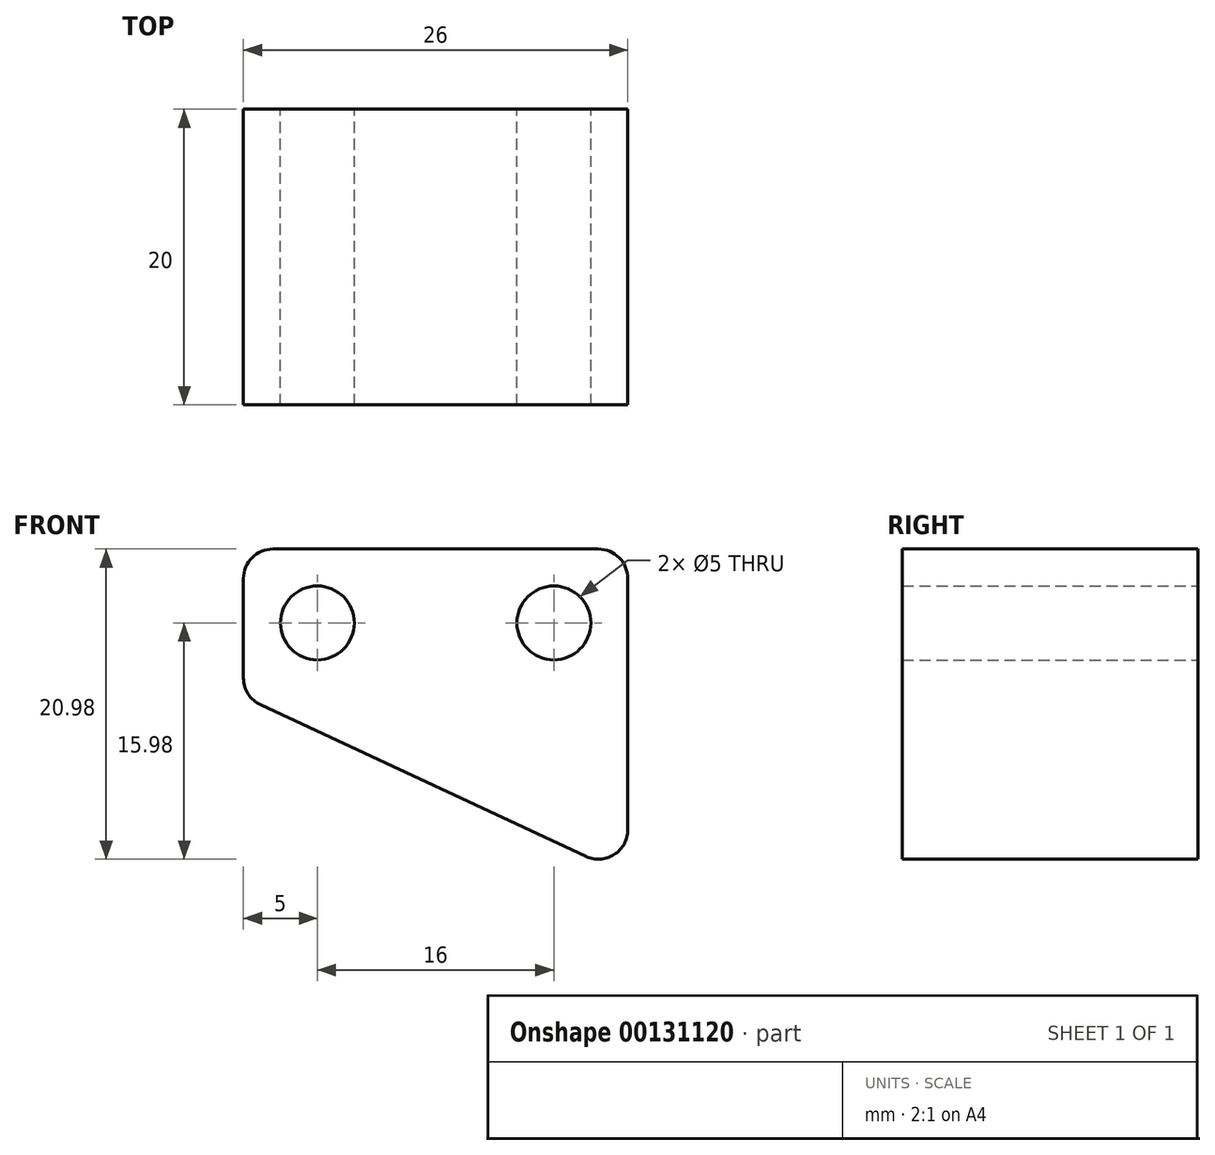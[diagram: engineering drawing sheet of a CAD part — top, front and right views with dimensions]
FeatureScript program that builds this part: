
annotation { "Feature Type Name" : "Feature", "Feature Type Description" : "" }
export const myFeature = defineFeature(function(context is Context, id is Id, definition is map)
    precondition{}
    {
        {
            var Q0;
            Q0=qCreatedBy(makeId("Front.planeOp"),FACE);
            var sketch = newSketch(context, id + "F0", { "sketchPlane" : qUnion([Q0])});
            skLineSegment(sketch, "E0", {"start": v(0, 0) * mm, "end": v(26, 0) * mm});
            skLineSegment(sketch, "E1", {"start": v(26, 0) * mm, "end": v(26, -22.12) * mm});
            skLineSegment(sketch, "E2", {"start": v(26, -22.12) * mm, "end": v(0, -10) * mm});
            skLineSegment(sketch, "E3", {"start": v(0, -10) * mm, "end": v(0, 0) * mm});
            skLineSegment(sketch, "E4", {"start": v(0, -5) * mm, "end": v(26, -5) * mm, "construction": true});
            skPoint(sketch, "E5", {"position": v(5, -5) * mm});
            skPoint(sketch, "E6", {"position": v(21, -5) * mm});
            skSolve(sketch);
        }
        {
            var Q0;
            Q0=makeQuery(id+"F0.imprint","IMPRINT",FACE,{"disambiguationData":[TD([[makeQuery(id+"F0.imprint","IMPRINT",EDGE,{"derivedFrom":sQuery(id+"F0.wireOp",EDGE,"E0")}),-1.0]])]});
            extrude(context, id + "F1", {"entities" : qUnion([Q0]), "depth" : 20 * mm});
        }
        {
            var Q0;
            Q0=sQuery(id+"F0.wireOp",VERTEX,"E5");
            var Q1;
            Q1=sQuery(id+"F0.wireOp",VERTEX,"E6");
            var Q2;
            Q2=makeQuery(id+"F1.opExtrude","SWEPT_BODY",BODY,{"disambiguationData":[OSD([sQuery(id+"F0.wireOp",EDGE,"E0"),sQuery(id+"F0.wireOp",EDGE,"E1"),sQuery(id+"F0.wireOp",EDGE,"E2"),sQuery(id+"F0.wireOp",EDGE,"E3")])]});
            hole(context, id + "F2", {"style" : HoleStyle.SIMPLE, "endStyle" : HoleEndStyle.THROUGH, "oppositeDirection" : true, "holeDiameter" : 5 * mm, "locations" : qUnion([Q0, Q1]), "scope" : qUnion([Q2]), "isTappedThrough" : true});
        }
        {
            var Q0;
            Q0=makeQuery(id+"F1.opExtrude","SWEPT_EDGE",EDGE,{"disambiguationData":[OSD([sQuery(id+"F0.wireOp",EDGE,"E1"),sQuery(id+"F0.wireOp",EDGE,"E2")])]});
            var Q1;
            Q1=makeQuery(id+"F1.opExtrude","SWEPT_EDGE",EDGE,{"disambiguationData":[OSD([sQuery(id+"F0.wireOp",EDGE,"E2"),sQuery(id+"F0.wireOp",EDGE,"E3")])]});
            var Q2;
            Q2=makeQuery(id+"F1.opExtrude","SWEPT_EDGE",EDGE,{"disambiguationData":[OSD([sQuery(id+"F0.wireOp",EDGE,"E0"),sQuery(id+"F0.wireOp",EDGE,"E3")])]});
            var Q3;
            Q3=makeQuery(id+"F1.opExtrude","SWEPT_EDGE",EDGE,{"disambiguationData":[OSD([sQuery(id+"F0.wireOp",EDGE,"E0"),sQuery(id+"F0.wireOp",EDGE,"E1")])]});
            fillet(context, id + "F3", {"entities" : qUnion([Q0, Q1, Q2, Q3]), "radius" : 2 * mm, "tangentPropagation" : true, "allowEdgeOverflow" : false});
        }
    });
